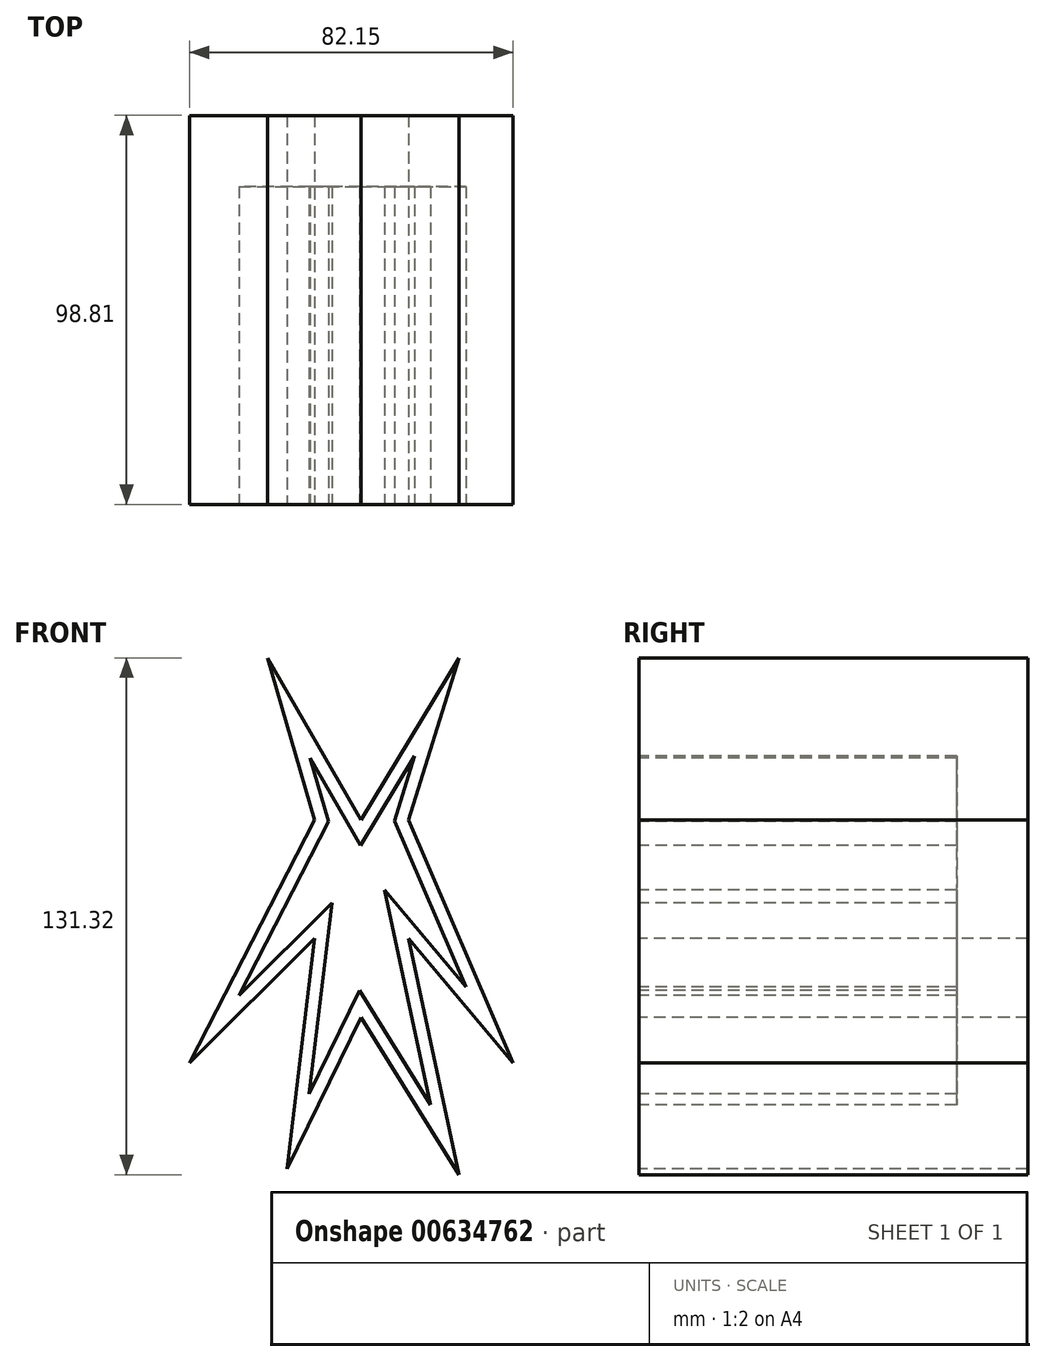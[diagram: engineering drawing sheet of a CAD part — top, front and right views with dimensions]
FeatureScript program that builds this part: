
annotation { "Feature Type Name" : "Feature", "Feature Type Description" : "" }
export const myFeature = defineFeature(function(context is Context, id is Id, definition is map)
    precondition{}
    {
        {
            var Q0;
            Q0=qCreatedBy(makeId("Front.planeOp"),FACE);
            var sketch = newSketch(context, id + "F0", { "sketchPlane" : qUnion([Q0])});
            skLineSegment(sketch, "E0", {"start": v(24.89, -60) * mm, "end": v(0, -20) * mm});
            skLineSegment(sketch, "E1", {"start": v(0, -20) * mm, "end": v(-18.78, -58.48) * mm});
            skLineSegment(sketch, "E2", {"start": v(24.89, -60) * mm, "end": v(12.06, 0) * mm});
            skLineSegment(sketch, "E3", {"start": v(-18.78, -58.48) * mm, "end": v(-11.76, 0) * mm});
            skLineSegment(sketch, "E4", {"start": v(-11.76, 0) * mm, "end": v(-43.52, -31.6) * mm});
            skLineSegment(sketch, "E5", {"start": v(-43.52, -31.6) * mm, "end": v(-11.76, 30.08) * mm});
            skLineSegment(sketch, "E6", {"start": v(12.06, 0) * mm, "end": v(24.89, -60) * mm});
            skLineSegment(sketch, "E7", {"start": v(12.06, 0) * mm, "end": v(38.63, -31.6) * mm});
            skLineSegment(sketch, "E8", {"start": v(38.63, -31.6) * mm, "end": v(12.06, 30.08) * mm});
            skLineSegment(sketch, "E9", {"start": v(12.06, 30.08) * mm, "end": v(24.89, 71.3) * mm});
            skLineSegment(sketch, "E10", {"start": v(24.89, 71.3) * mm, "end": v(0, 30.08) * mm});
            skLineSegment(sketch, "E11", {"start": v(-11.76, 30.08) * mm, "end": v(-23.67, 71.3) * mm});
            skLineSegment(sketch, "E12", {"start": v(-23.67, 71.3) * mm, "end": v(0, 30.08) * mm});
            skSolve(sketch);
        }
        {
            var Q0;
            Q0=makeQuery(id+"F0.imprint","IMPRINT",FACE,{"disambiguationData":[TD([[makeQuery(id+"F0.imprint","IMPRINT",EDGE,{"derivedFrom":sQuery(id+"F0.wireOp",EDGE,"E0")}),-1.0]])]});
            extrude(context, id + "F1", {"entities" : qUnion([Q0]), "oppositeDirection" : true, "depth" : 98.8 * mm, "offsetDistance" : 25.4 * mm});
        }
        {
            var Q0;
            Q0=makeQuery(id+"F1.opExtrude","CAP_FACE",FACE,{"disambiguationData":[OSD([sQuery(id+"F0.wireOp",EDGE,"E0"),sQuery(id+"F0.wireOp",EDGE,"E1"),sQuery(id+"F0.wireOp",EDGE,"E3"),sQuery(id+"F0.wireOp",EDGE,"E4"),sQuery(id+"F0.wireOp",EDGE,"E5"),sQuery(id+"F0.wireOp",EDGE,"E6"),sQuery(id+"F0.wireOp",EDGE,"E7"),sQuery(id+"F0.wireOp",EDGE,"E8"),sQuery(id+"F0.wireOp",EDGE,"E9"),sQuery(id+"F0.wireOp",EDGE,"E10"),sQuery(id+"F0.wireOp",EDGE,"E11"),sQuery(id+"F0.wireOp",EDGE,"E12")])],"isStart":true});
            var sketch = newSketch(context, id + "F2", { "sketchPlane" : qUnion([Q0])});
            skLineSegment(sketch, "E13.0", {"start": v(13.65, 46.3) * mm, "end": v(-0.07, 23.57) * mm});
            skLineSegment(sketch, "E13.1", {"start": v(-7.34, 9.05) * mm, "end": v(-13.17, -39.46) * mm});
            skLineSegment(sketch, "E13.2", {"start": v(-30.98, -14.47) * mm, "end": v(-7.34, 9.05) * mm});
            skLineSegment(sketch, "E13.3", {"start": v(-8.22, 29.74) * mm, "end": v(-30.98, -14.47) * mm});
            skLineSegment(sketch, "E13.4", {"start": v(-12.9, 45.9) * mm, "end": v(-8.22, 29.74) * mm});
            skLineSegment(sketch, "E13.5", {"start": v(-13.17, -39.46) * mm, "end": v(-0.35, -13.2) * mm});
            skLineSegment(sketch, "E13.6", {"start": v(-0.07, 23.57) * mm, "end": v(-12.9, 45.9) * mm});
            skLineSegment(sketch, "E13.7", {"start": v(-0.35, -13.2) * mm, "end": v(17.7, -42.22) * mm});
            skLineSegment(sketch, "E13.8", {"start": v(17.7, -42.22) * mm, "end": v(6.06, 12.27) * mm});
            skLineSegment(sketch, "E13.9", {"start": v(6.06, 12.27) * mm, "end": v(26.73, -12.31) * mm});
            skLineSegment(sketch, "E13.10", {"start": v(26.73, -12.31) * mm, "end": v(8.55, 29.9) * mm});
            skLineSegment(sketch, "E13.11", {"start": v(8.55, 29.9) * mm, "end": v(13.65, 46.3) * mm});
            skSolve(sketch);
        }
        {
            var Q0;
            Q0=makeQuery(id+"F2.imprint","IMPRINT",FACE,{"disambiguationData":[TD([[makeQuery(id+"F2.imprint","IMPRINT",EDGE,{"derivedFrom":sQuery(id+"F2.wireOp",EDGE,"E13.0")}),1.0]])]});
            extrude(context, id + "F3", {"entities" : qUnion([Q0]), "operationType" : NewBodyOperationType.REMOVE, "oppositeDirection" : true, "depth" : 80.77 * mm, "offsetDistance" : 25.4 * mm});
        }
    });
